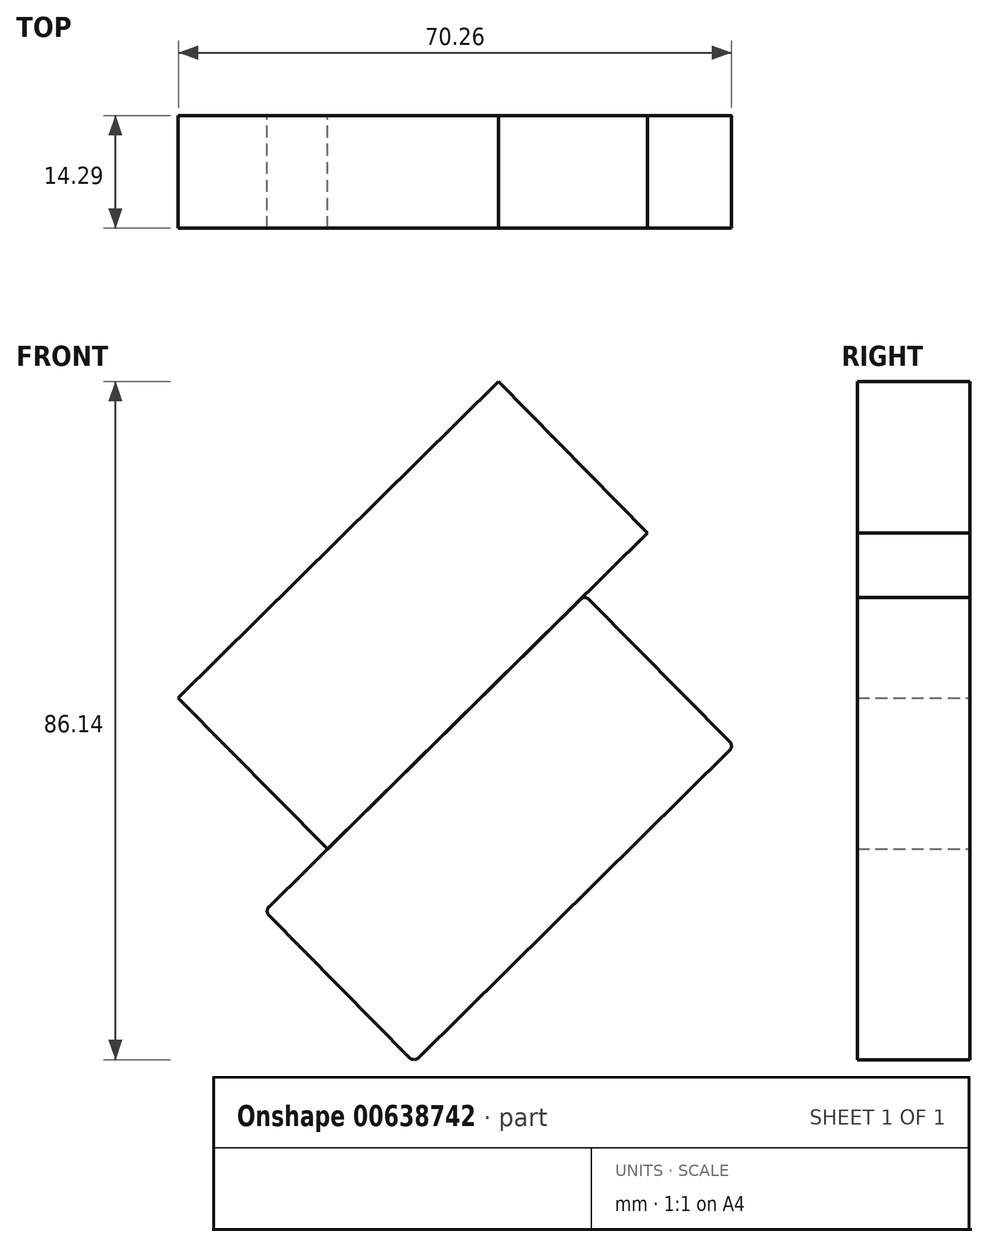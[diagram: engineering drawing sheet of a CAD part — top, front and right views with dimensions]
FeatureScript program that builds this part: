
annotation { "Feature Type Name" : "Feature", "Feature Type Description" : "" }
export const myFeature = defineFeature(function(context is Context, id is Id, definition is map)
    precondition{}
    {
        {
            var Q0;
            Q0=qCreatedBy(makeId("Front.planeOp"),FACE);
            var sketch = newSketch(context, id + "F0", { "sketchPlane" : qUnion([Q0])});
            skLineSegment(sketch, "E0.bottom", {"start": v(0, 0) * mm, "end": v(662.43, 0) * mm});
            skLineSegment(sketch, "E0.top", {"start": v(0, 229.37) * mm, "end": v(662.43, 229.37) * mm});
            skLineSegment(sketch, "E0.left", {"start": v(0, 0) * mm, "end": v(0, 229.37) * mm});
            skLineSegment(sketch, "E0.right", {"start": v(662.43, 0) * mm, "end": v(662.43, 229.37) * mm});
            skSolve(sketch);
        }
        {
            var Q0;
            Q0=qCreatedBy(makeId("Front.planeOp"),FACE);
            var sketch = newSketch(context, id + "F1", { "sketchPlane" : qUnion([Q0])});
            skLineSegment(sketch, "E1", {"start": v(182.56, 93.22) * mm, "end": v(223.23, 133.38) * mm});
            skLineSegment(sketch, "E2", {"start": v(223.23, 133.38) * mm, "end": v(242.19, 114.17) * mm});
            skLineSegment(sketch, "E3", {"start": v(242.19, 114.17) * mm, "end": v(201.53, 74.02) * mm});
            skLineSegment(sketch, "E4", {"start": v(201.53, 74.02) * mm, "end": v(182.56, 93.22) * mm});
            skLineSegment(sketch, "E5", {"start": v(192.04, 83.62) * mm, "end": v(232.7, 123.77) * mm, "construction": true});
            skCircle(sketch, "E6", {"center": v(201.36, 92.82) * mm, "radius": 2.38 * mm});
            skCircle(sketch, "E7", {"center": v(208.14, 99.51) * mm, "radius": 2.38 * mm});
            skCircle(sketch, "E8", {"center": v(214.92, 106.2) * mm, "radius": 2.38 * mm});
            skCircle(sketch, "E9", {"center": v(221.7, 112.9) * mm, "radius": 2.38 * mm});
            skLineSegment(sketch, "E10", {"start": v(192.04, 83.62) * mm, "end": v(199.67, 91.15) * mm, "construction": true});
            skLineSegment(sketch, "E11", {"start": v(232.7, 123.77) * mm, "end": v(223.39, 114.57) * mm});
            skLineSegment(sketch, "E12", {"start": v(201.36, 92.82) * mm, "end": v(208.14, 99.51) * mm});
            skLineSegment(sketch, "E13", {"start": v(214.92, 106.2) * mm, "end": v(221.7, 112.9) * mm});
            skLineSegment(sketch, "E14", {"start": v(125.8, 109.55) * mm, "end": v(218.3, 109.55) * mm});
            skLineSegment(sketch, "E15", {"start": v(125.8, 96.17) * mm, "end": v(204.75, 96.17) * mm});
            skLineSegment(sketch, "E16", {"start": v(223.39, 114.57) * mm, "end": v(232.7, 123.77) * mm});
            skLineSegment(sketch, "E17", {"start": v(212.26, 160.48) * mm, "end": v(231.23, 141.28) * mm});
            skLineSegment(sketch, "E18", {"start": v(231.23, 141.28) * mm, "end": v(190.56, 101.12) * mm});
            skLineSegment(sketch, "E19", {"start": v(190.56, 101.12) * mm, "end": v(171.6, 120.32) * mm});
            skLineSegment(sketch, "E20", {"start": v(181.08, 110.72) * mm, "end": v(221.74, 150.88) * mm, "construction": true});
            skLineSegment(sketch, "E21", {"start": v(181.08, 110.72) * mm, "end": v(190.4, 119.92) * mm});
            skCircle(sketch, "E22", {"center": v(190.4, 119.92) * mm, "radius": 2.38 * mm});
            skCircle(sketch, "E23", {"center": v(197.18, 126.61) * mm, "radius": 2.38 * mm});
            skCircle(sketch, "E24", {"center": v(203.95, 133.3) * mm, "radius": 2.38 * mm});
            skCircle(sketch, "E25", {"center": v(210.73, 140) * mm, "radius": 2.38 * mm});
            skLineSegment(sketch, "E26", {"start": v(190.4, 119.92) * mm, "end": v(197.18, 126.61) * mm});
            skLineSegment(sketch, "E27", {"start": v(186.3, 123.27) * mm, "end": v(193.79, 123.27) * mm});
            skLineSegment(sketch, "E28", {"start": v(203.95, 133.3) * mm, "end": v(210.73, 140) * mm});
            skLineSegment(sketch, "E29", {"start": v(241.33, 136.65) * mm, "end": v(207.34, 136.65) * mm});
            skLineSegment(sketch, "E30", {"start": v(171.6, 120.32) * mm, "end": v(212.26, 160.48) * mm});
            skSolve(sketch);
        }
        {
            var Q0;
            Q0=qCreatedBy(makeId("Front.planeOp"),FACE);
            var sketch = newSketch(context, id + "F2", { "sketchPlane" : qUnion([Q0])});
            skLineSegment(sketch, "E31.0", {"start": v(223.23, 133.38) * mm, "end": v(242.19, 114.17) * mm});
            skLineSegment(sketch, "E32.0", {"start": v(242.19, 114.17) * mm, "end": v(201.53, 74.02) * mm});
            skLineSegment(sketch, "E33.0", {"start": v(201.53, 74.02) * mm, "end": v(182.56, 93.22) * mm});
            skLineSegment(sketch, "E34.0", {"start": v(182.56, 93.22) * mm, "end": v(223.23, 133.38) * mm});
            skSolve(sketch);
        }
        {
            var Q0;
            Q0 = qSketchRegion(id + "F2", true);
            extrude(context, id + "F3", {"entities" : qUnion([Q0]), "depth" : 14.29 * mm, "offsetDistance" : 25.4 * mm});
        }
        {
            var Q0;
            Q0=makeQuery(id+"F3.opExtrude","SWEPT_EDGE",EDGE,{"disambiguationData":[OSD([sQuery(id+"F2.wireOp",EDGE,"E32.0"),sQuery(id+"F2.wireOp",EDGE,"E33.0")])]});
            var Q1;
            Q1=makeQuery(id+"F3.opExtrude","SWEPT_EDGE",EDGE,{"disambiguationData":[OSD([sQuery(id+"F2.wireOp",EDGE,"E33.0"),sQuery(id+"F2.wireOp",EDGE,"E34.0")])]});
            var Q2;
            Q2=makeQuery(id+"F3.opExtrude","SWEPT_EDGE",EDGE,{"disambiguationData":[OSD([sQuery(id+"F2.wireOp",EDGE,"E31.0"),sQuery(id+"F2.wireOp",EDGE,"E32.0")])]});
            var Q3;
            Q3=makeQuery(id+"F3.opExtrude","SWEPT_EDGE",EDGE,{"disambiguationData":[OSD([sQuery(id+"F2.wireOp",EDGE,"E31.0"),sQuery(id+"F2.wireOp",EDGE,"E34.0")])]});
            fillet(context, id + "F4", {"entities" : qUnion([Q0, Q1, Q2, Q3]), "radius" : 0.8 * mm, "tangentPropagation" : true, "allowEdgeOverflow" : false});
        }
        {
            var Q0;
            Q0=qCreatedBy(makeId("Front.planeOp"),FACE);
            var sketch = newSketch(context, id + "F5", { "sketchPlane" : qUnion([Q0])});
            skLineSegment(sketch, "E35.0", {"start": v(212.26, 160.48) * mm, "end": v(231.23, 141.28) * mm});
            skLineSegment(sketch, "E36.0", {"start": v(171.6, 120.32) * mm, "end": v(212.26, 160.48) * mm});
            skLineSegment(sketch, "E37.0", {"start": v(190.56, 101.12) * mm, "end": v(171.6, 120.32) * mm});
            skLineSegment(sketch, "E38.0", {"start": v(231.23, 141.28) * mm, "end": v(190.56, 101.12) * mm});
            skSolve(sketch);
        }
        {
            var Q0;
            Q0 = qSketchRegion(id + "F5", true);
            extrude(context, id + "F6", {"entities" : qUnion([Q0]), "depth" : 14.29 * mm, "offsetDistance" : 25.4 * mm});
        }
    });
